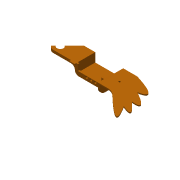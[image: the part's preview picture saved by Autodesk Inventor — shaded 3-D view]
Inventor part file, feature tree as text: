
AUTODESK INVENTOR PART (.ipt)
format: ipt  version: 2016 (Build 200138000, 138)  size: 307,712 bytes
history: native  units: in
note: dims shown in document units (in); Inventor stores cm internally (conversion verified against a paired STEP export)
features: sketch x11, reference x11, extrude x7, fillet x5, hole x4, chamfer x4, projected_geometry x2, other x1
ambient origin geometry x8: Origin, YZ Plane, XZ Plane, XY Plane, X Axis, Y Axis, Z Axis, Center Point
bodies: Solid1 (feature_tree)
feature tree (45):
  other  "skeleton.ipt"
  extrude  "Extrusion1"  Depth=0.0394in
  extrude  "Extrusion2"  Depth=0.0197in
  extrude  "Extrusion3"  Depth=1.2598in TaperAngle=0.0deg
  hole  "Hole1"  [1 undecoded]
  hole  "Hole2"  [1 undecoded]
  chamfer  "Chamfer1"  Distance=0.1181in
  hole  "Hole3"  [1 undecoded]
  chamfer  "Chamfer2"  Distance=0.0394in Angle=45.0deg
  extrude  "Extrusion4"  Depth=0.1181in
  extrude  "Extrusion5"  Depth=0.1181in
  chamfer  "Chamfer3"  Distance=0.9843in
  fillet  "Fillet1"  Radius=1.7717in
  fillet  "Fillet2"  Radius=2.3622in
  fillet  "Fillet4"  Radius=3.7402in
  fillet  "Fillet7"  Radius=0.0787in
  extrude  "Extrusion6"  Depth=0.1181in
  hole  "Hole4"  [1 undecoded]
  chamfer  "Chamfer4"  Distance=0.1181in
  fillet  "Fillet9"  Radius=0.4331in
  extrude  "Extrusion7"  Depth=0.1181in
  sketch  "Sketch1"  dims[d0=0.0394in d1=0.0197in]
  reference  "Reference1"
  reference  "Reference2"
  reference  "Reference3"
  reference  "Reference4"
  reference  "Reference5"
  reference  "Reference6"
  sketch  "Sketch3"  dims[d2=0.0197in d3=0.0197in]
  reference  "Reference7"
  reference  "Reference8"
  reference  "Reference9"
  projected_geometry  "Projected Loop1"
  sketch  "Sketch4"  dims[d4=0.0984in d5=1.2598in d6=0.0in]
  sketch  "Sketch5"  dims[d7=0.0394in d8=0.0394in]
  sketch  "Sketch6"  dims[d9=0.0394in d10=0.1181in d11=0.1181in d12=0.0in]
  reference  "Reference10"
  reference  "Reference11"
  sketch  "Sketch7"  dims[d13=0.1969in d14=0.0in d15=0.3937in]
  sketch  "Sketch8"  dims[d17=4.7244in]
  sketch  "Sketch9"  dims[d18=0.9055in]
  sketch  "Sketch10"  dims[d19=1.9291in]
  sketch  "Sketch11"  dims[d20=0.4724in d21=0.2362in d22=0.1575in d23=0.0787in d24=90.0deg d25=0.315in d26=0.8108in]
  sketch  "Sketch12"  dims[d27=0.1024in d28=0.2362in d29=0.1575in d30=0.0787in d31=90.0deg d32=0.315in d33=0.8108in d34=0.0394in d35=0.0787in d36=45.0deg d37=3.3465in d38=3.7402in d39=0.9843in d40=1.7717in d41=2.3622in d42=3.7402in d43=0.0787in d44=0.0in d45=2.0472in d46=0.1299in d47=0.2362in d48=0.1575in d49=0.0787in d50=90.0deg d51=0.315in d52=0.8108in d53=0.0591in d54=0.0787in d55=45.0deg d56=0.1181in d58=0.4331in d59=0.0in d60=0.0787in d61=0.4331in d62=0.1181in d63=0.0787in d64=45.0deg d65=0.7874in d66=0.3937in d68=0.3937in d71=0.2756in d72=0.1181in d73=0.0in d75=0.1299in d76=0.2362in d77=0.1575in d78=0.0787in d79=90.0deg d80=0.315in d81=0.8108in d82=0.0394in d83=0.0787in d84=45.0deg d85=0.0394in d86=0.1181in d87=0.1969in d88=0.1181in d89=0.0in]
  projected_geometry  "Projected Loop2"
note: 4 required parameter values undecoded (feature->parameter linkage not recoverable at this tier; creation-order binding heuristic only, values carry confidence <= 0.55)
